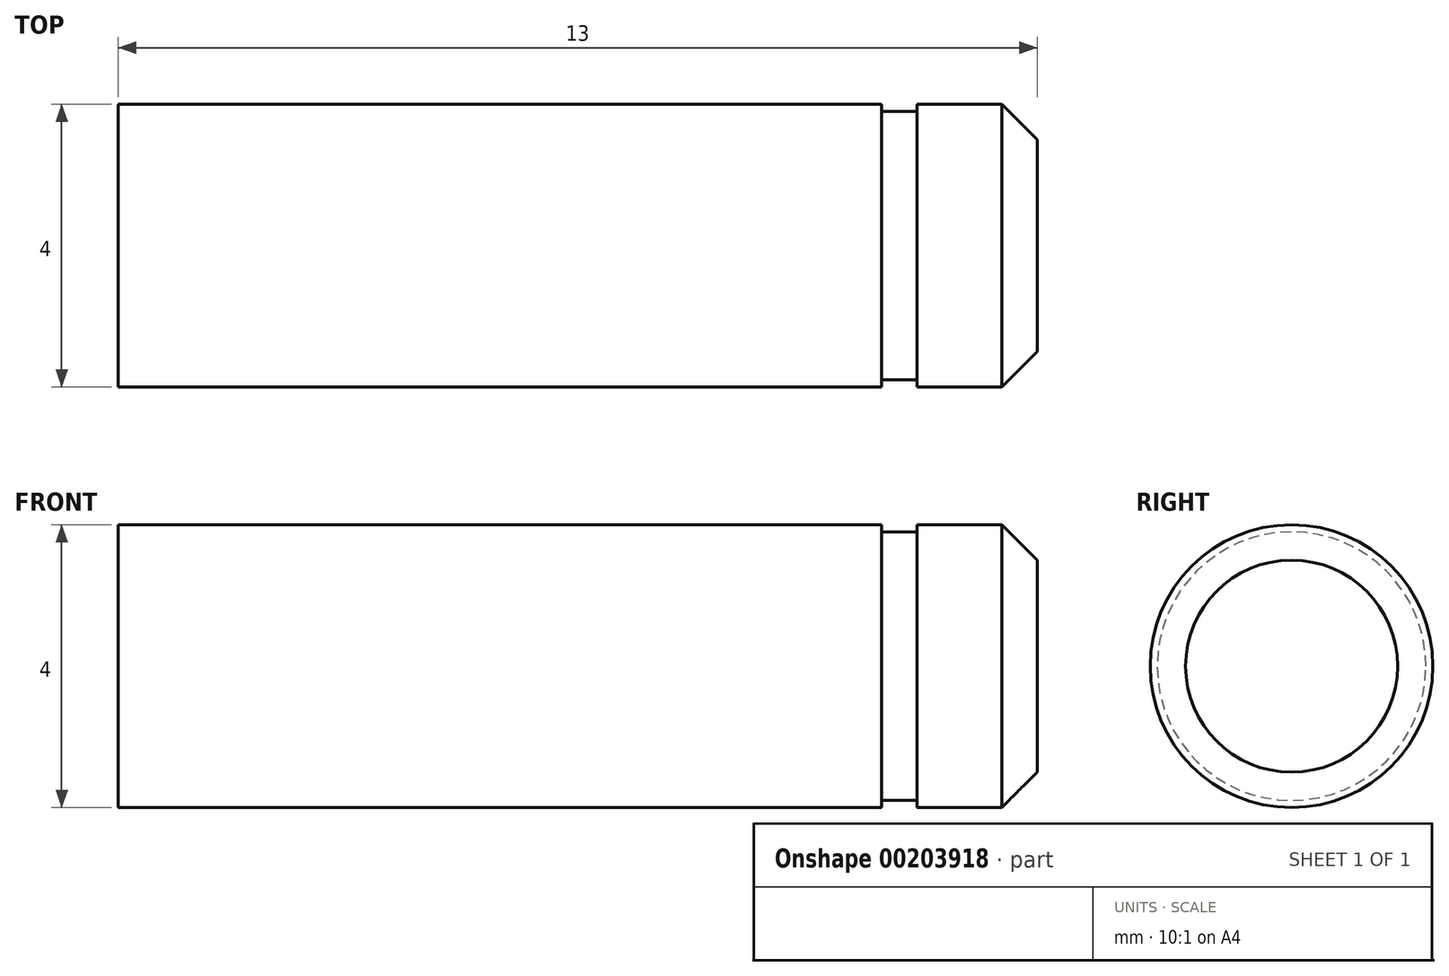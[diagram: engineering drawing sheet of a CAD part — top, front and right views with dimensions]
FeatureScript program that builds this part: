
annotation { "Feature Type Name" : "Feature", "Feature Type Description" : "" }
export const myFeature = defineFeature(function(context is Context, id is Id, definition is map)
    precondition{}
    {
        {
            var Q0;
            Q0=qCreatedBy(makeId("Front.planeOp"),FACE);
            var sketch = newSketch(context, id + "F0", { "sketchPlane" : qUnion([Q0])});
            skLineSegment(sketch, "E0", {"start": v(-38.73, 0) * mm, "end": v(41.27, 0) * mm, "construction": true});
            skLineSegment(sketch, "E1", {"start": v(0, 0) * mm, "end": v(0, 2) * mm});
            skLineSegment(sketch, "E2", {"start": v(0, 2) * mm, "end": v(10.8, 2) * mm});
            skLineSegment(sketch, "E3", {"start": v(10.8, 2) * mm, "end": v(10.8, 1.9) * mm});
            skLineSegment(sketch, "E4", {"start": v(10.8, 1.9) * mm, "end": v(11.3, 1.9) * mm});
            skLineSegment(sketch, "E5", {"start": v(11.3, 1.9) * mm, "end": v(11.3, 2) * mm});
            skLineSegment(sketch, "E6", {"start": v(11.3, 2) * mm, "end": v(13, 2) * mm});
            skLineSegment(sketch, "E7", {"start": v(13, 2) * mm, "end": v(13, 0) * mm});
            skLineSegment(sketch, "E8", {"start": v(0, 0) * mm, "end": v(13, 0) * mm});
            skSolve(sketch);
        }
        {
            var Q0;
            Q0=qSketchRegion(id+"F0",true);
            var Q1;
            Q1=sQuery(id+"F0.wireOp",EDGE,"E0");
            revolve(context, id + "F1", {"entities" : qUnion([Q0]), "axis" : qUnion([Q1]), "revolveType" : RevolveType.FULL});
        }
        {
            var Q0;
            Q0=makeQuery(id+"F1.opRevolve","SWEPT_EDGE",EDGE,{"disambiguationData":[OSD([sQuery(id+"F0.wireOp",EDGE,"E6"),sQuery(id+"F0.wireOp",EDGE,"E7")])]});
            chamfer(context, id + "F2", {"entities" : qUnion([Q0]), "width" : 0.5 * mm, "tangentPropagation" : true});
        }
    });
